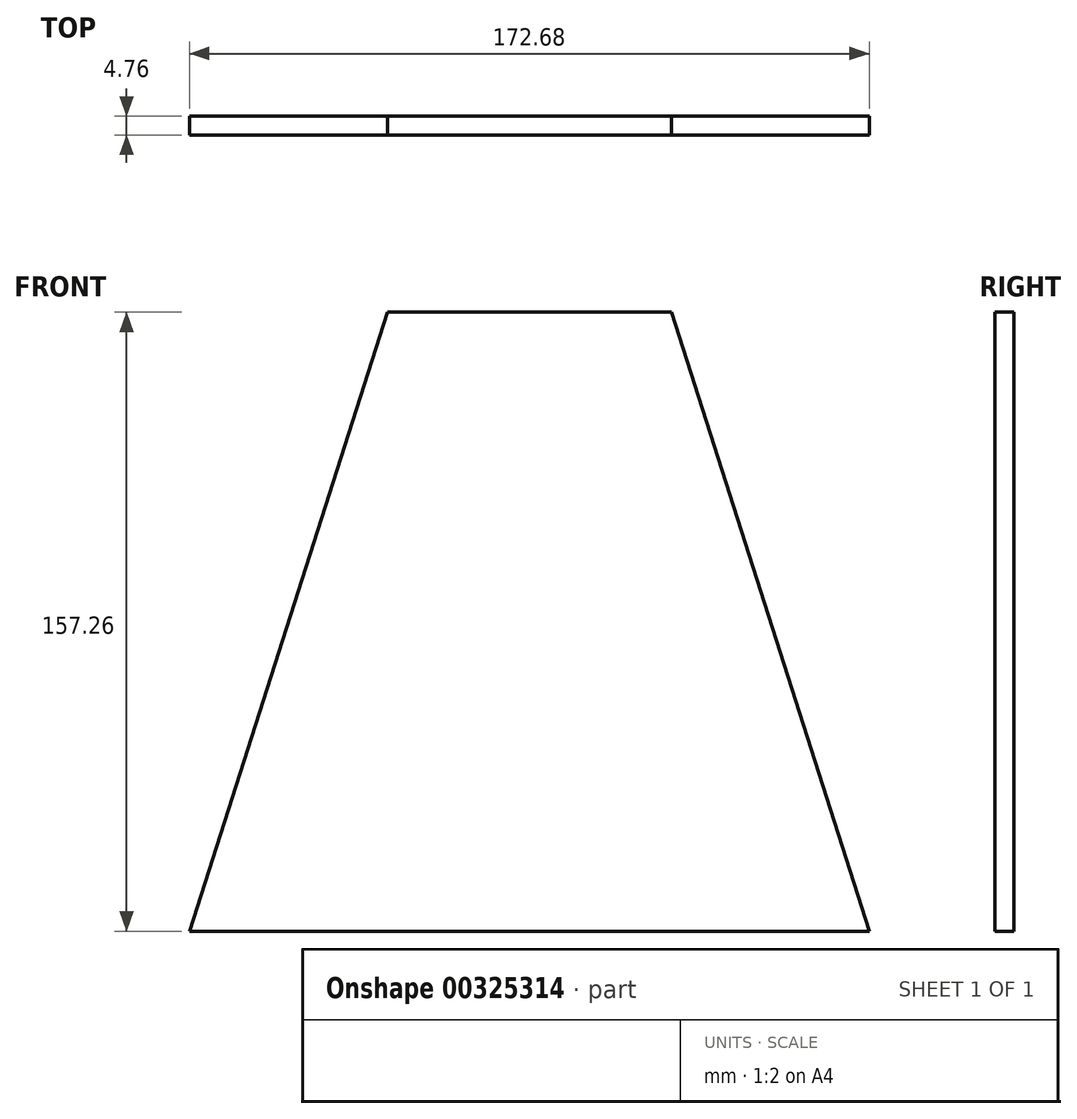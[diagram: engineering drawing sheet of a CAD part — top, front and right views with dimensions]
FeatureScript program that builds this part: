
annotation { "Feature Type Name" : "Feature", "Feature Type Description" : "" }
export const myFeature = defineFeature(function(context is Context, id is Id, definition is map)
    precondition{}
    {
        {
            var Q0;
            Q0=qCreatedBy(makeId("Front.planeOp"),FACE);
            var sketch = newSketch(context, id + "F0", { "sketchPlane" : qUnion([Q0])});
            skLineSegment(sketch, "E0", {"start": v(0, 0) * mm, "end": v(172.68, 0) * mm});
            skLineSegment(sketch, "E1", {"start": v(172.68, 0) * mm, "end": v(122.4, 157.26) * mm});
            skLineSegment(sketch, "E2", {"start": v(122.4, 157.26) * mm, "end": v(50.28, 157.26) * mm});
            skLineSegment(sketch, "E3", {"start": v(50.28, 157.26) * mm, "end": v(0, 0) * mm});
            skLineSegment(sketch, "E4", {"start": v(86.34, 0) * mm, "end": v(86.34, 157.26) * mm, "construction": true});
            skLineSegment(sketch, "E5", {"start": v(5.38, 16.81) * mm, "end": v(167.3, 16.81) * mm, "construction": true});
            skLineSegment(sketch, "E6", {"start": v(41.89, 131) * mm, "end": v(130.79, 131) * mm, "construction": true});
            skSolve(sketch);
        }
        {
            var Q0;
            Q0 = qSketchRegion(id + "F0", true);
            extrude(context, id + "F1", {"entities" : qUnion([Q0]), "depth" : 4.76 * mm});
        }
    });
